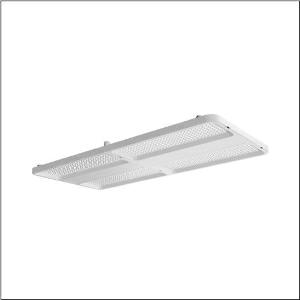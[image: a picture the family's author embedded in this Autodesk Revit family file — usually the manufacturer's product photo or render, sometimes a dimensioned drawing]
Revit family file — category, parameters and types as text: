
# Revit family: highbay_21_maxi_52hn12db3pda
name_source: partatom
category: Lighting Fixtures
units: mm (PartAtom-declared; Revit-internal decimal feet)

## family parameters
Cut with Voids When Loaded = No
Host = Face
Light Source = No
Part Type = Normal
Room Calculation Point = No
Round Connector Dimension = Use Diameter
Shared = No

## types (1)
- --- (1 x LED, 5350 lm, 31.4 W, 3000K)
    Apparent Load = 31 VA
    CIE Flux Codes = 90 98 100 100 100
    Color Rendering = 80
    Color Temperature = 3000K
    Default Elevation = 1800 mm
    Description = high bay luminaire Highbay 21 maxi; direct symmetric wide distribution, light control with lens of PMMA; UGR ≤ 22 (X = 4H | Y = 8H | S = 0.25H | reflection values 70/50/20); luminous flux: 34.690lm; light colour: 830, colour temperature: 3000K, MacAdam ≤ 3 SDCM (initial), colour rendering: CRI > 80; luminous efficacy: 175,5lm/W; rated service life: 75.000h (L80) at AT= ta max; control: DALI 2; luminaire connection: terminal, 5-pole, max. 2.5mm² (cable entry for one cable, Ø 8.5..16mm); mains connection: 230..240V, AC/DC 0/50..60Hz; connected load: 197,7W; protection rating (complete): IP66; insulation class (complete): insulation class I (protective earthing); protection symbol: D; impact resistance: IK08; certification: CE, ENEC, VDE, UKCA; luminaire for central battery installations according to EN 60598-2-22, internal wiring halogen-free; luminaire LABS conformity tested according to VDMA 24364:2018-05; Suitable for use in the food industry according to the specifications of IFS-Food, HACCP and/or BRC; housing frame of high-performance plastic PA6, matt traffic white (RAL 9016); cover of PMMA; dimension (LxWxH): 946 x 442 x 72mm; permissible operating ambient temperature: -40..+60°C (reducing of maximum allowable ambient temperature of 5°C with ceiling mounting); packaging unit: 1 piece; (delivery without accessories; please order mounting accessories separately)
    Height = 72 mm  [stored 0.23622 ft]
    Lamp = 1 x LED
    Lamp Light Flux = 5350 lm
    Lamp Power = 31.4 W
    Lamp count = 1
    Length = 946 mm
    Luminous efficacy = 170 lm/W
    Manufacturer = Siteco
    ModVariant = No
    Model = 52HN12DB3PDA
    Mounting Place = Ceiling
    Mounting Type = Pendant
    Number of Poles = 1
    OnlyDefault = Yes
    Power Factor = 1
    Product Name = Highbay 21 maxi
    Product group = high bay luminaire
    ProductGroupID = 902
    Protection Class = Protection class I
    Protection Degree = IP 66
    RLX_Detail_Level = 1
    RLX_Emergency_Light_Flux = 0 lm
    RLX_Emergency_Type = 0
    RLX_Emergency_Type_DB = No
    RlxData = <blob elided: 127961 chars, md5=8bed2b88>
    Socket = socket
    Standby Power = 0 W
    System Light Flux = 5350 lm
    System Power = 31 W
    Type Comments = : DC mode (central or group accumulator) initial emergency light level
    Type Image = l_1363244.jpg
    URL = http://relux.com
    VarID = @adj_004887
    Voltage = 0 V
    Weight = 0.00 kg
    Width = 442 mm

note: [stored X ft] marks values corroborated as IEEE doubles in the binary element streams (Revit-internal decimal feet)

## geometry (parser evidence)
native form markers: Blend x4, Sweep x11
no freeform markers — native parametric forms only
